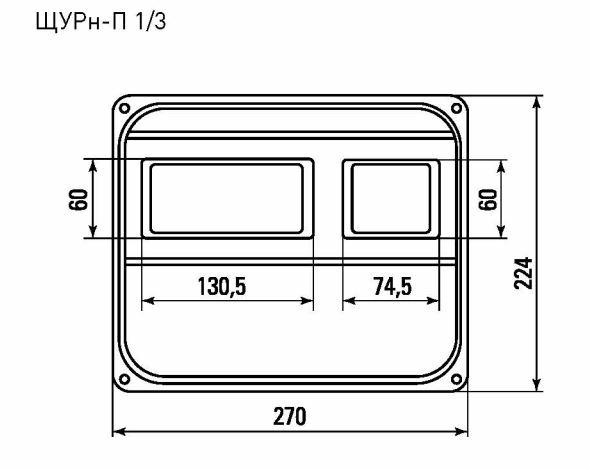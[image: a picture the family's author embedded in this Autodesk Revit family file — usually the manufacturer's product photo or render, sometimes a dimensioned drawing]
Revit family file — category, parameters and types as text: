
# Revit family: EKF_EE_Щит_Inox_AISI 304_IP66_У1_PROxima
name_source: partatom
category: Электрооборудование
units: mm (PartAtom-declared; Revit-internal decimal feet)

## family parameters
Всегда вертикально = Да
На основе рабочей плоскости = Нет
Общий = Нет
При загрузке вырезать с полостями = Нет
Размер круглого соединителя = Использовать диаметр
Тип детали = Силовой щит
Точка расчета площади = Да

## types (17) — shared parameters
ADSK_Единица измерения = компл.
ADSK_Завод-изготовитель = EKF
ADSK_Количество = 1
ADSK_Марка = Щит Inox AISI 304 IP66 У1
ADSK_Материал = RAL 7035_Сталь
ADSK_Обозначение = Щит Inox AISI 304 IP66 У1
Изготовитель = EKF
Серия номенклатуры = PROxima
Степень защиты IP = IP66
ТВ = EKF
Тип установки = Навесной
zero-valued in all types: Количество DIN-реек, Количество модулей на DIN-рейке, Максимальное количество модулей

## per-type parameters (varying)
| type | ADSK_Код изделия | ADSK_Масса | ADSK_Наименование | ADSK_Размер_Высота | ADSK_Размер_Глубина | ADSK_Размер_Ширина | Описание | Тип |
| Щит из нержавеющей стали "Inox" AISI 304 (1000х600х300) IP66 У1 EKF PROxima | mb-inox-1063 | 34.3 | Щит из нержавеющей стали Inox AISI 304 (1000х600х300) IP66 У1 EKF PROxima | 1000 мм | 300 мм | 600 мм | Щит из нержавеющей стали Inox AISI 304 (1000х600х300) IP66 У1 EKF PROxima | 120 мм |
| Щит из нержавеющей стали "Inox" AISI 304 (1200х800х300) IP66 У1 EKF PROxima | mb-inox-1283 | 51.3 | Щит из нержавеющей стали Inox AISI 304 (1200х800х300) IP66 У1 EKF PROxima | 1200 мм | 300 мм | 800 мм | Щит из нержавеющей стали Inox AISI 304 (1200х800х300) IP66 У1 EKF PROxima | 121 мм |
| Щит из нержавеющей стали "Inox" AISI 304 (250х300х150) IP66 У1 EKF PROxima | mb-inox-231 | 3.4 | Щит из нержавеющей стали Inox AISI 304 (250х300х150) IP66 У1 EKF PROxima | 250 мм | 150 мм | 300 мм | Щит из нержавеющей стали Inox AISI 304 (250х300х150) IP66 У1 EKF PROxima | 122 мм |
| Щит из нержавеющей стали "Inox" AISI 304 (300х200х150) IP66 У1 EKF PROxima | mb-inox-3215 | 2.8 | Щит из нержавеющей стали Inox AISI 304 (300х200х150) IP66 У1 EKF PROxima | 300 мм | 150 мм | 200 мм | Щит из нержавеющей стали Inox AISI 304 (300х200х150) IP66 У1 EKF PROxima | 123 мм |
| Щит из нержавеющей стали "Inox" AISI 304 (300х250х150) IP66 У1 EKF PROxima | mb-inox-321 | 3.3 | Щит из нержавеющей стали Inox AISI 304 (300х250х150) IP66 У1 EKF PROxima | 300 мм | 150 мм | 250 мм | Щит из нержавеющей стали Inox AISI 304 (300х250х150) IP66 У1 EKF PROxima | 124 мм |
| Щит из нержавеющей стали "Inox" AISI 304 (400х200х150) IP66 У1 EKF PROxima | mb-inox-421 | 3.6 | Щит из нержавеющей стали Inox AISI 304 (400х200х150) IP66 У1 EKF PROxima | 400 мм | 150 мм | 200 мм | Щит из нержавеющей стали Inox AISI 304 (400х200х150) IP66 У1 EKF PROxima | 125 мм |
| Щит из нержавеющей стали "Inox" AISI 304 (400х300х150) IP66 У1 EKF PROxima | mb-inox-431 | 5 | Щит из нержавеющей стали Inox AISI 304 (400х300х150) IP66 У1 EKF PROxima | 400 мм | 150 мм | 300 мм | Щит из нержавеющей стали Inox AISI 304 (400х300х150) IP66 У1 EKF PROxima | 126 мм |
| Щит из нержавеющей стали "Inox" AISI 304 (400х300х200) IP66 У1 EKF PROxima | mb-inox-432 | 5.6 | Щит из нержавеющей стали Inox AISI 304 (400х300х200) IP66 У1 EKF PROxima | 400 мм | 200 мм | 300 мм | Щит из нержавеющей стали Inox AISI 304 (400х300х200) IP66 У1 EKF PROxima | 127 мм |
| Щит из нержавеющей стали "Inox" AISI 304 (400х400х210) IP66 У1 EKF PROxima | mb-inox-442 | 7.3 | Щит из нержавеющей стали Inox AISI 304 (400х400х210) IP66 У1 EKF PROxima | 400 мм | 210 мм | 400 мм | Щит из нержавеющей стали Inox AISI 304 (400х400х210) IP66 У1 EKF PROxima | 128 мм |
| Щит из нержавеющей стали "Inox" AISI 304 (500х400х210) IP66 У1 EKF PROxima | mb-inox-5421 | 9.6 | Щит из нержавеющей стали Inox AISI 304 (500х400х210) IP66 У1 EKF PROxima | 500 мм | 210 мм | 400 мм | Щит из нержавеющей стали Inox AISI 304 (500х400х210) IP66 У1 EKF PROxima | 129 мм |
| Щит из нержавеющей стали "Inox" AISI 304 (500х400х250) IP66 У1 EKF PROxima | mb-inox-542 | 10.2 | Щит из нержавеющей стали Inox AISI 304 (500х400х250) IP66 У1 EKF PROxima | 500 мм | 250 мм | 400 мм | Щит из нержавеющей стали Inox AISI 304 (500х400х250) IP66 У1 EKF PROxima | 130 мм |
| Щит из нержавеющей стали "Inox" AISI 304 (600х400х200) IP66 У1 EKF PROxima | mb-inox-642 | 11.1 | Щит из нержавеющей стали Inox AISI 304 (600х400х200) IP66 У1 EKF PROxima | 600 мм | 200 мм | 400 мм | Щит из нержавеющей стали Inox AISI 304 (600х400х200) IP66 У1 EKF PROxima | 131 мм |
| Щит из нержавеющей стали "Inox" AISI 304 (600х500х250) IP66 У1 EKF PROxima | mb-inox-652 | 14.4 | Щит из нержавеющей стали Inox AISI 304 (600х500х250) IP66 У1 EKF PROxima | 600 мм | 250 мм | 500 мм | Щит из нержавеющей стали Inox AISI 304 (600х500х250) IP66 У1 EKF PROxima | 132 мм |
| Щит из нержавеющей стали "Inox" AISI 304 (700х500х200) IP66 У1 EKF PROxima | mb-inox-752 | 15.6 | Щит из нержавеющей стали Inox AISI 304 (700х500х200) IP66 У1 EKF PROxima | 700 мм | 200 мм | 500 мм | Щит из нержавеющей стали Inox AISI 304 (700х500х200) IP66 У1 EKF PROxima | 133 мм |
| Щит из нержавеющей стали "Inox" AISI 304 (700х500х250) IP66 У1 EKF PROxima | mb-inox-7525 | 16.5 | Щит из нержавеющей стали Inox AISI 304 (700х500х250) IP66 У1 EKF PROxima | 700 мм | 250 мм | 500 мм | Щит из нержавеющей стали Inox AISI 304 (700х500х250) IP66 У1 EKF PROxima | 134 мм |
| Щит из нержавеющей стали "Inox" AISI 304 (800х600х250) IP66 У1 EKF PROxima | mb-inox-862 | 26.6 | Щит из нержавеющей стали Inox AISI 304 (800х600х250) IP66 У1 EKF PROxima | 800 мм | 250 мм | 600 мм | Щит из нержавеющей стали Inox AISI 304 (800х600х250) IP66 У1 EKF PROxima | 135 мм |
| Щит из нержавеющей стали "Inox" AISI 304 (800х600х300) IP66 У1 EKF PROxima | mb-inox-863 | 28.3 | Щит из нержавеющей стали Inox AISI 304 (800х600х300) IP66 У1 EKF PROxima | 800 мм | 300 мм | 600 мм | Щит из нержавеющей стали Inox AISI 304 (800х600х300) IP66 У1 EKF PROxima | 136 мм |
